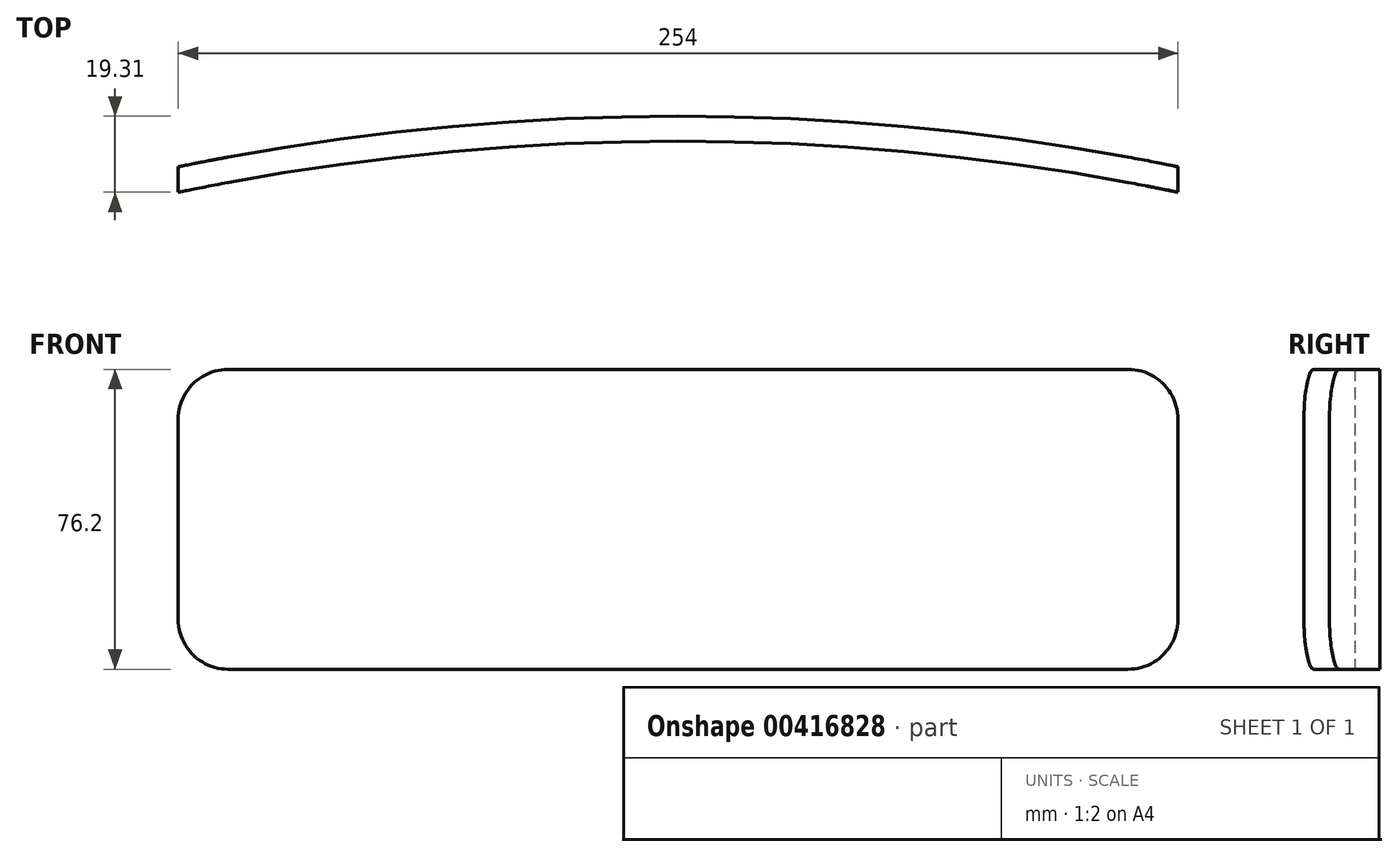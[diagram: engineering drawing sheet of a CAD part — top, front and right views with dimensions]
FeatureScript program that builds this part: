
annotation { "Feature Type Name" : "Feature", "Feature Type Description" : "" }
export const myFeature = defineFeature(function(context is Context, id is Id, definition is map)
    precondition{}
    {
        {
            var Q0;
            Q0=qCreatedBy(makeId("Top.planeOp"),FACE);
            var sketch = newSketch(context, id + "F0", { "sketchPlane" : qUnion([Q0])});
            skLineSegment(sketch, "E0.bottom", {"start": v(0, 0) * mm, "end": v(1270, 0) * mm});
            skLineSegment(sketch, "E0.top", {"start": v(0, 1270) * mm, "end": v(1270, 1270) * mm});
            skLineSegment(sketch, "E0.left", {"start": v(0, 0) * mm, "end": v(0, 1270) * mm});
            skLineSegment(sketch, "E0.right", {"start": v(1270, 0) * mm, "end": v(1270, 1270) * mm});
            skCircle(sketch, "E1", {"center": v(635, 0) * mm, "radius": 635 * mm});
            skLineSegment(sketch, "E2.bottom", {"start": v(508, 762) * mm, "end": v(762, 762) * mm});
            skLineSegment(sketch, "E2.top", {"start": v(508, 508) * mm, "end": v(762, 508) * mm});
            skLineSegment(sketch, "E2.left", {"start": v(508, 762) * mm, "end": v(508, 508) * mm});
            skLineSegment(sketch, "E2.right", {"start": v(762, 762) * mm, "end": v(762, 508) * mm});
            skCircle(sketch, "E3.0", {"center": v(635, 0) * mm, "radius": 628.65 * mm});
            skSolve(sketch);
        }
        {
            var Q0;
            {var subQ0=sQuery(id+"F0.wireOp",EDGE,"E2.right");var subQ1=sQuery(id+"F0.wireOp",EDGE,"E1");var subQ2=makeQuery(id+"F0.imprint","INTERSECT",VERTEX,{"derivedFrom":[subQ1,subQ0]});Q0=makeQuery(id+"F0.imprint","IMPRINT",FACE,{"disambiguationData":[TD([[makeQuery(id+"F0.imprint","IMPRINT",EDGE,{"disambiguationData":[TD([[subQ2,-1.0]])],"derivedFrom":subQ1}),1.0]])]});}
            extrude(context, id + "F1", {"entities" : qUnion([Q0]), "depth" : 76.2 * mm, "offsetDistance" : 25.4 * mm});
        }
        {
            var Q0;
            Q0=makeQuery(id+"F1.opExtrude","CAP_EDGE",EDGE,{"disambiguationData":[OSD([sQuery(id+"F0.wireOp",EDGE,"E2.left")])],"isStart":false});
            var Q1;
            Q1=makeQuery(id+"F1.opExtrude","CAP_EDGE",EDGE,{"disambiguationData":[OSD([sQuery(id+"F0.wireOp",EDGE,"E2.left")])],"isStart":true});
            var Q2;
            Q2=makeQuery(id+"F1.opExtrude","CAP_EDGE",EDGE,{"disambiguationData":[OSD([sQuery(id+"F0.wireOp",EDGE,"E2.right")])],"isStart":false});
            var Q3;
            Q3=makeQuery(id+"F1.opExtrude","CAP_EDGE",EDGE,{"disambiguationData":[OSD([sQuery(id+"F0.wireOp",EDGE,"E2.right")])],"isStart":true});
            fillet(context, id + "F2", {"entities" : qUnion([Q0, Q1, Q2, Q3]), "tangentPropagation" : true, "radius" : 12.7 * mm, "defaultsChanged" : true, "vertexSettings" : [], "allowEdgeOverflow" : false});
        }
    });
